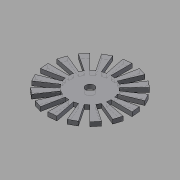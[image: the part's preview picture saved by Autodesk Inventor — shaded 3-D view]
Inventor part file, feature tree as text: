
AUTODESK INVENTOR PART (.ipt)
format: ipt  version: 2015 (Build 190159000, 159)  size: 173,056 bytes
history: native  units: in
note: dims shown in document units (in); Inventor stores cm internally (conversion verified against a paired STEP export)
features: other x3, sketch x1
ambient origin geometry x8: Origin, YZ Plane, XZ Plane, XY Plane, X Axis, Y Axis, Z Axis, Center Point
bodies: Solid1 (feature_tree)
feature tree (4):
  other  "encoder_MIR2.ipt"
  other  "Solid1::encoder_MIR2.ipt"
  other  "TaggingFeature1"
  sketch  "Sketch1"  dims[d0=0.3937in]
